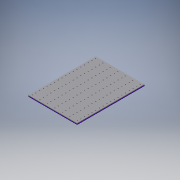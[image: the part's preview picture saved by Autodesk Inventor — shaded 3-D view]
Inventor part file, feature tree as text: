
AUTODESK INVENTOR PART (.ipt)
format: ipt  version: 2016 (Build 200138000, 138)  size: 275,456 bytes
history: native  units: mm
features: reference x112, extrude x1, sketch x1
ambient origin geometry x8: Origin, YZ Plane, XZ Plane, XY Plane, X Axis, Y Axis, Z Axis, Center Point
bodies: Body1 (feature_tree)
feature tree (114):
  extrude  "Extrusion8"  Depth=4.0mm
  sketch  "Sketch1"  dims[d0=208.0mm d1=288.0mm d17=32.0mm d18=32.0mm d19=32.0mm d20=32.0mm d21=32.0mm d22=32.0mm d23=8.0mm d25=9.6mm d26=9.6mm d27=8.0mm d29=9.6mm d30=8.0mm d31=14.4mm d32=16.0mm d33=14.4mm d34=14.4mm d35=16.0mm d36=14.4mm d37=16.0mm d38=16.0mm d39=9.6mm d40=8.0mm d41=4.0mm d42=0.0mm]
  reference  "Reference4"
  reference  "Reference8"
  reference  "Reference9"
  reference  "Reference10"
  reference  "Reference11"
  reference  "Reference12"
  reference  "Reference13"
  reference  "Reference14"
  reference  "Reference15"
  reference  "Reference16"
  reference  "Reference17"
  reference  "Reference18"
  reference  "Reference19"
  reference  "Reference20"
  reference  "Reference21"
  reference  "Reference22"
  reference  "Reference23"
  reference  "Reference24"
  reference  "Reference25"
  reference  "Reference26"
  reference  "Reference27"
  reference  "Reference28"
  reference  "Reference29"
  reference  "Reference30"
  reference  "Reference31"
  reference  "Reference32"
  reference  "Reference33"
  reference  "Reference34"
  reference  "Reference35"
  reference  "Reference36"
  reference  "Reference37"
  reference  "Reference38"
  reference  "Reference39"
  reference  "Reference40"
  reference  "Reference41"
  reference  "Reference42"
  reference  "Reference43"
  reference  "Reference44"
  reference  "Reference45"
  reference  "Reference46"
  reference  "Reference47"
  reference  "Reference48"
  reference  "Reference49"
  reference  "Reference50"
  reference  "Reference51"
  reference  "Reference52"
  reference  "Reference53"
  reference  "Reference54"
  reference  "Reference55"
  reference  "Reference56"
  reference  "Reference57"
  reference  "Reference58"
  reference  "Reference59"
  reference  "Reference60"
  reference  "Reference61"
  reference  "Reference62"
  reference  "Reference63"
  reference  "Reference64"
  reference  "Reference65"
  reference  "Reference66"
  reference  "Reference67"
  reference  "Reference68"
  reference  "Reference69"
  reference  "Reference70"
  reference  "Reference71"
  reference  "Reference72"
  reference  "Reference73"
  reference  "Reference74"
  reference  "Reference75"
  reference  "Reference76"
  reference  "Reference77"
  reference  "Reference78"
  reference  "Reference79"
  reference  "Reference80"
  reference  "Reference81"
  reference  "Reference82"
  reference  "Reference83"
  reference  "Reference84"
  reference  "Reference85"
  reference  "Reference86"
  reference  "Reference87"
  reference  "Reference88"
  reference  "Reference89"
  reference  "Reference90"
  reference  "Reference91"
  reference  "Reference92"
  reference  "Reference93"
  reference  "Reference94"
  reference  "Reference95"
  reference  "Reference96"
  reference  "Reference97"
  reference  "Reference98"
  reference  "Reference99"
  reference  "Reference100"
  reference  "Reference101"
  reference  "Reference102"
  reference  "Reference103"
  reference  "Reference104"
  reference  "Reference105"
  reference  "Reference106"
  reference  "Reference107"
  reference  "Reference108"
  reference  "Reference109"
  reference  "Reference110"
  reference  "Reference111"
  reference  "Reference112"
  reference  "Reference113"
  reference  "Reference114"
  reference  "Reference115"
  reference  "Reference116"
  reference  "Reference117"
  reference  "Reference118"
